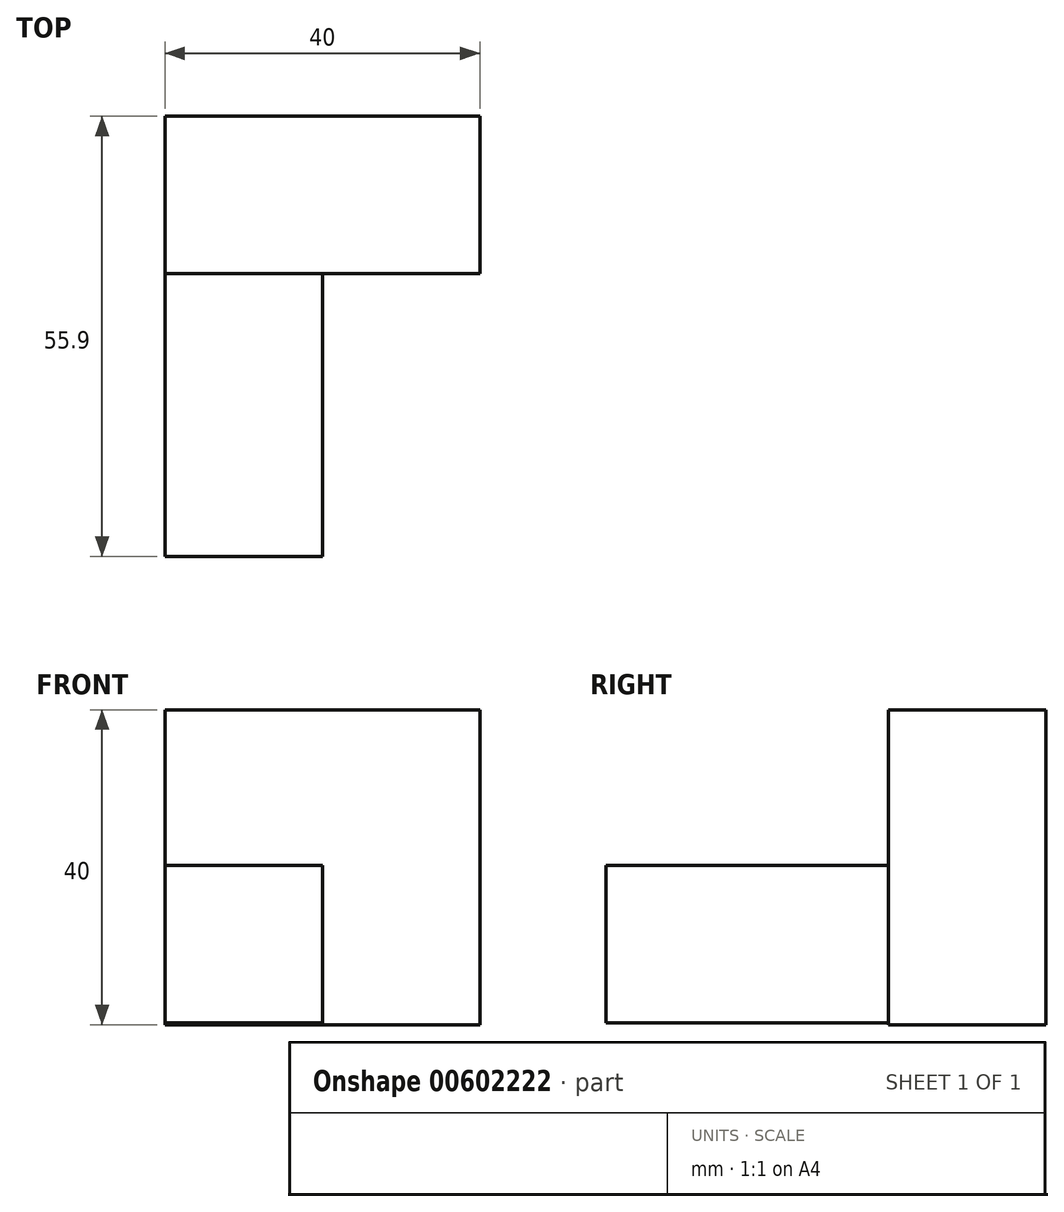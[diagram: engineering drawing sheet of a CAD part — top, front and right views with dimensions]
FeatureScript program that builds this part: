
annotation { "Feature Type Name" : "Feature", "Feature Type Description" : "" }
export const myFeature = defineFeature(function(context is Context, id is Id, definition is map)
    precondition{}
    {
        {
            var Q0;
            Q0=qCreatedBy(makeId("Front.planeOp"),FACE);
            var sketch = newSketch(context, id + "F0", { "sketchPlane" : qUnion([Q0])});
            skLineSegment(sketch, "E0", {"start": v(-57.52, 54.86) * mm, "end": v(-57.52, 34.86) * mm});
            skLineSegment(sketch, "E1", {"start": v(-57.52, 54.86) * mm, "end": v(-37.52, 54.86) * mm});
            skLineSegment(sketch, "E2", {"start": v(-37.52, 54.86) * mm, "end": v(-37.52, 34.86) * mm});
            skLineSegment(sketch, "E3", {"start": v(-57.52, 34.86) * mm, "end": v(-37.52, 34.86) * mm});
            skSolve(sketch);
        }
        {
            var Q0;
            Q0 = qSketchRegion(id + "F0", true);
            extrude(context, id + "F1", {"entities" : qUnion([Q0]), "depth" : 55.9 * mm, "offsetDistance" : 25 * mm});
        }
        {
            var Q0;
            Q0=qCreatedBy(makeId("Front.planeOp"),FACE);
            var sketch = newSketch(context, id + "F2", { "sketchPlane" : qUnion([Q0])});
            skLineSegment(sketch, "E4", {"start": v(-57.52, 34.61) * mm, "end": v(-57.52, 74.61) * mm});
            skLineSegment(sketch, "E5", {"start": v(-57.52, 74.61) * mm, "end": v(-17.52, 74.61) * mm});
            skLineSegment(sketch, "E6", {"start": v(-17.52, 74.61) * mm, "end": v(-17.52, 34.61) * mm});
            skLineSegment(sketch, "E7", {"start": v(-17.52, 34.61) * mm, "end": v(-57.52, 34.61) * mm});
            skSolve(sketch);
        }
        {
            var Q0;
            Q0=makeQuery(id+"F2.imprint","IMPRINT",FACE,{"disambiguationData":[TD([[makeQuery(id+"F2.imprint","IMPRINT",EDGE,{"derivedFrom":sQuery(id+"F2.wireOp",EDGE,"E4")}),-1.0]])]});
            extrude(context, id + "F3", {"entities" : qUnion([Q0]), "operationType" : NewBodyOperationType.ADD, "depth" : 20 * mm, "offsetDistance" : 25 * mm});
        }
    });
